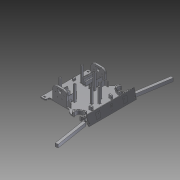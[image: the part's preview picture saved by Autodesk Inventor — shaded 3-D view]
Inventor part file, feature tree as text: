
AUTODESK INVENTOR PART (.ipt)
format: ipt  version: 2011 SP2 (Build 150309200, 309)  size: 1,400,320 bytes
history: native  units: mm
features: extrude x33, sketch x19, projected_geometry x14, fillet x12, mirror x2, plane x1, chamfer x1, hole x1
ambient origin geometry x8: Origin, YZ Plane, XZ Plane, XY Plane, X Axis, Y Axis, Z Axis, Center Point
feature tree (83):
  sketch  "Sketch1"  dims[d0=200.0mm d1=200.0mm]
  extrude  "Extrusion3"  Depth=200.0mm
  extrude  "Extrusion4"  Depth=10.5mm
  extrude  "Extrusion5"  Depth=6.5mm
  extrude  "Extrusion6"  Depth=53.3mm
  extrude  "Extrusion7"  Depth=26.65mm
  sketch  "Sketch4"  dims[d6=6.5mm d8=53.3mm]
  extrude  "Extrusion8"  Depth=5.0mm
  extrude  "Extrusion9"  Depth=5.0mm
  extrude  "Extrusion10"  Depth=4.4mm
  plane  "Work Plane1"
  mirror  "Mirror1"
  sketch  "Sketch9"  dims[d9=53.3mm d10=26.65mm]
  sketch  "Sketch10"  dims[d11=26.65mm d13=5.0mm]
  extrude  "Extrusion16"  Depth=8.0mm
  extrude  "Extrusion17"  Depth=8.0mm
  extrude  "Extrusion18"  Depth=60.0mm
  extrude  "Extrusion19"  Depth=39.0mm
  extrude  "Extrusion20"  Depth=3.65mm
  extrude  "Extrusion21"  Depth=1.5mm
  extrude  "Extrusion22"  Depth=6.6mm
  sketch  "Sketch13"  dims[d18=4.4mm d19=8.0mm]
  extrude  "Extrusion26"  Depth=6.6mm
  extrude  "Extrusion27"  Depth=3.5mm
  extrude  "Extrusion30"  Depth=5.0mm
  extrude  "Extrusion32"  Depth=46.7mm
  extrude  "Extrusion33"  Depth=4.0mm TaperAngle=0.0deg
  extrude  "Extrusion34"  Depth=11.0mm TaperAngle=0.0deg
  chamfer  "Chamfer2"  Distance=55.0mm
  fillet  "Fillet1"  Radius=13.0mm
  extrude  "Extrusion35"  Depth=38.0mm
  extrude  "Extrusion36"  Depth=36.8mm
  sketch  "Sketch21"  dims[d28=1.6mm d29=3.65mm d30=3.65mm]
  extrude  "Extrusion37"  Depth=7.0mm
  extrude  "Extrusion39"  Depth=3.0mm
  extrude  "Extrusion40"  Depth=15.5mm
  fillet  "Fillet2"  Radius=60.0mm
  sketch  "Sketch28"  dims[d44=60.0mm d45=6.6mm]
  extrude  "Extrusion48"  Depth=55.0mm TaperAngle=0.0deg
  extrude  "Extrusion49"  Depth=2.0mm
  extrude  "Extrusion42"  Depth=2.0mm
  extrude  "Extrusion44"  Depth=3.65mm
  fillet  "Fillet4"  Radius=3.65mm
  mirror  "Mirror3"
  fillet  "Fillet3"  Radius=55.0mm
  extrude  "Extrusion45"  Depth=36.8mm
  sketch  "Sketch30"  dims[d49=12.061mm d50=5.0mm]
  extrude  "Extrusion46"  Depth=36.0mm
  extrude  "Extrusion47"  Depth=40.0mm TaperAngle=0.0deg
  hole  "Hole1"  [1 undecoded]
  fillet  "Fillet5"  Radius=23.0mm
  fillet  "Fillet6"  Radius=23.35mm
  fillet  "Fillet7"  Radius=6.15mm
  fillet  "Fillet8"  Radius=2.8mm
  fillet  "Fillet9"  Radius=2.8mm
  fillet  "Fillet10"  Radius=2.8mm
  fillet  "Fillet11"  Radius=2.8mm
  fillet  "Fillet12"  Radius=32.757mm
  sketch  "Sketch2"  dims[d2=10.5mm d3=10.5mm]
  sketch  "Sketch3"  dims[d4=57.861mm d5=6.5mm]
  projected_geometry  "Projected Loop1"
  projected_geometry  "Projected Loop7"
  sketch  "Sketch11"  dims[d14=5.0mm d15=5.0mm]
  sketch  "Sketch12"  dims[d16=6.15mm d17=4.4mm]
  projected_geometry  "Projected Loop8"
  sketch  "Sketch15"  dims[d20=5.0mm d21=8.0mm]
  projected_geometry  "Projected Loop9"
  sketch  "Sketch18"  dims[d22=5.0mm d23=60.0mm]
  projected_geometry  "Projected Loop11"
  sketch  "Sketch20"  dims[d25=138.0mm d27=39.0mm]
  projected_geometry  "Projected Loop12"
  sketch  "Sketch25"  dims[d31=3.0mm d32=0.5mm d34=1.5mm d36=5.0mm]
  sketch  "Sketch27"  dims[d37=3.0mm d38=5.0mm d39=8.15mm d41=6.6mm d42=1.5mm d43=0.5mm]
  projected_geometry  "Projected Loop16"
  sketch  "Sketch29"  dims[d47=11.6mm d48=3.5mm]
  sketch  "Sketch31"  dims[d56=8.15mm d57=46.7mm d58=4.0mm d59=0.0mm d60=11.0mm d61=0.0mm d62=55.0mm d63=0.0mm d64=13.0mm d65=38.0mm d66=36.8mm d67=7.0mm d68=3.0mm d69=15.5mm d70=60.0mm d72=360.0deg d74=55.0mm d75=0.0mm d76=2.0mm d77=2.0mm d78=3.65mm d79=3.65mm d80=55.0mm d81=0.0mm d82=36.8mm d83=36.0mm d84=40.0mm d85=0.0mm d86=40.0mm d87=0.0mm d88=23.0mm d89=0.0mm d90=23.35mm d91=6.15mm d119=2.8mm d120=2.8mm d121=2.8mm d122=2.8mm d135=32.757mm d136=32.757mm d137=80.957mm d138=80.957mm d139=27.264mm d140=20.564mm d141=34.936mm d142=35.936mm d143=2.0mm d144=11.0mm d145=11.0mm d146=2.0mm d147=11.0mm d148=11.0mm d149=2.0mm d150=2.0mm d155=6.0mm d156=6.0mm d157=6.0mm d158=6.0mm d159=3.0mm d160=3.0mm d161=3.0mm d162=3.0mm d163=6.0mm d164=6.0mm d165=3.0mm d166=3.0mm d167=6.0mm d168=6.0mm d169=3.0mm d170=3.0mm d181=3.0mm d182=2.5mm d184=0.0mm d185=0.0mm d186=200.0mm d187=0.0mm d188=200.0mm d189=0.0mm d190=58.0mm d191=0.0mm d192=18.0mm d193=0.0mm d194=40.0mm d195=0.0mm d196=1.570796mm d197=1.570796mm d198=220.0mm d199=220.0mm d200=10.0mm d201=10.0mm d202=5.0mm d203=7.0mm d204=0.0mm d205=0.0mm d215=32.1mm d231=5.0mm d233=12.0mm d234=0.0mm d239=20.0mm d240=0.0mm d256=6.0mm d257=167.0mm d258=6.2mm d259=6.0mm d260=0.0mm d262=22.75mm d266=10.0mm d267=38.9mm d268=5.5mm d269=32.1mm d272=10.0mm d273=12.2mm d276=12.0mm d277=0.0mm d278=28.5mm d279=10.3mm d280=0.0mm d281=5.0mm d282=0.0mm d283=0.5mm d284=5.3mm d285=45.0deg d286=1.0mm d287=5.0mm d288=0.0mm d289=3.0mm d290=3.0mm d291=10.0mm d292=0.0mm d293=6.15mm d294=4.4mm d295=2.0mm d296=3.0mm d297=10.0mm d298=0.0mm d306=41.0mm d307=0.0mm d308=6.0mm d309=6.0mm d310=2.575mm d311=2.575mm d312=2.0mm d313=2.0mm d315=8.956377mm d316=161.0mm d317=10.0mm d318=7.0mm d319=0.0mm d320=32.5mm d335=32.5mm d336=7.0mm d337=12.0mm d338=9.25mm d339=-0.872665mm d343=1.0mm d344=9.25mm d345=-0.872665mm d346=8.0mm d347=4.0mm d348=10.0mm d349=20.0mm d350=0.0mm d351=179.0mm d352=0.0mm d353=179.0mm d354=0.0mm d355=1.5mm d356=3.5mm d357=3.5mm d358=89.5mm d359=89.5mm d360=5.0mm d361=17.5mm d362=2.0mm d363=6.0mm d364=3.0mm d365=2.0mm d366=90.0deg d367=2.0mm d368=3.665191mm d369=6.0mm d370=6.0mm d371=6.0mm d372=6.0mm d373=6.0mm d376=6.0mm d377=2.0mm d378=2.0mm d379=2.0mm d380=3.0mm d382=3.0mm d383=3.0mm d384=3.0mm d386=55.0mm d387=0.0mm d388=40.0mm d389=0.0mm d390=26.0mm d391=69.0mm d392=48.0mm d393=3.0mm d394=13.0mm d395=13.0mm d396=3.0mm d397=1.0mm d398=0.5mm d399=0.5mm d400=1.0mm d401=0.5mm d402=1.0mm d403=15.0mm d404=1.0mm]
  projected_geometry  "Projected Loop17"
  projected_geometry  "Projected Loop18"
  projected_geometry  "Projected Loop19"
  projected_geometry  "Projected Loop20"
  projected_geometry  "Projected Loop21"
  projected_geometry  "Projected Loop22"
  projected_geometry  "Projected Loop23"
note: 1 required parameter value undecoded (feature->parameter linkage not recoverable at this tier; creation-order binding heuristic only, values carry confidence <= 0.55)
